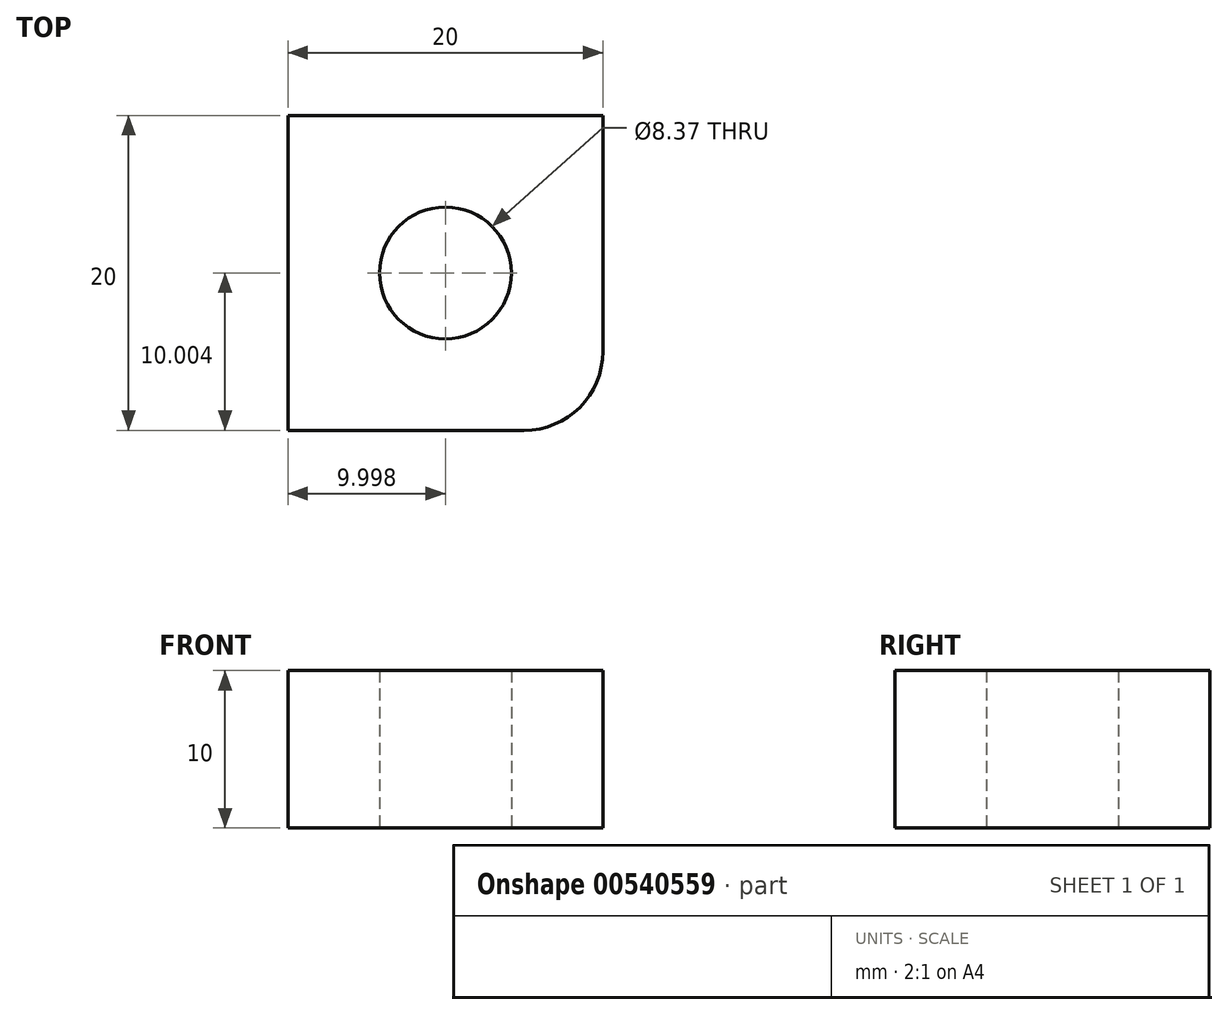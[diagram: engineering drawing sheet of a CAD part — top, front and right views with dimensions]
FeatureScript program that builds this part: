
annotation { "Feature Type Name" : "Feature", "Feature Type Description" : "" }
export const myFeature = defineFeature(function(context is Context, id is Id, definition is map)
    precondition{}
    {
        {
            var Q0;
            Q0=qCreatedBy(makeId("Top.planeOp"),FACE);
            var sketch = newSketch(context, id + "F0", { "sketchPlane" : qUnion([Q0])});
            skLineSegment(sketch, "E0.bottom", {"start": v(-19.75, 16.55) * mm, "end": v(0.25, 16.55) * mm});
            skLineSegment(sketch, "E0.top", {"start": v(-19.75, -3.45) * mm, "end": v(-4.75, -3.45) * mm});
            skLineSegment(sketch, "E0.left", {"start": v(-19.75, 16.55) * mm, "end": v(-19.75, -3.45) * mm});
            skLineSegment(sketch, "E0.right", {"start": v(0.25, 16.55) * mm, "end": v(0.25, 1.55) * mm});
            skPoint(sketch, "E1.visualSharp", {"position": v(0.25, -3.45) * mm});
            skArc(sketch, "E1.filletArc", {"start": v(-4.75, -3.45) * mm, "mid": v(-1.22, -1.98) * mm, "end": v(0.25, 1.55) * mm});
            skCircle(sketch, "E2", {"center": v(-9.75, 6.55) * mm, "radius": 4.19 * mm});
            skPoint(sketch, "E2.centerSnap0", {"position": v(-9.75, 16.55) * mm});
            skPoint(sketch, "E2.centerSnap1", {"position": v(-19.75, 6.55) * mm});
            skSolve(sketch);
        }
        {
            var Q0;
            Q0=makeQuery(id+"F0.imprint","IMPRINT",FACE,{"disambiguationData":[TD([[makeQuery(id+"F0.imprint","IMPRINT",EDGE,{"derivedFrom":sQuery(id+"F0.wireOp",EDGE,"E0.bottom")}),-1.0]])]});
            extrude(context, id + "F1", {"entities" : qUnion([Q0]), "depth" : 10 * mm, "offsetDistance" : 25 * mm});
        }
    });
